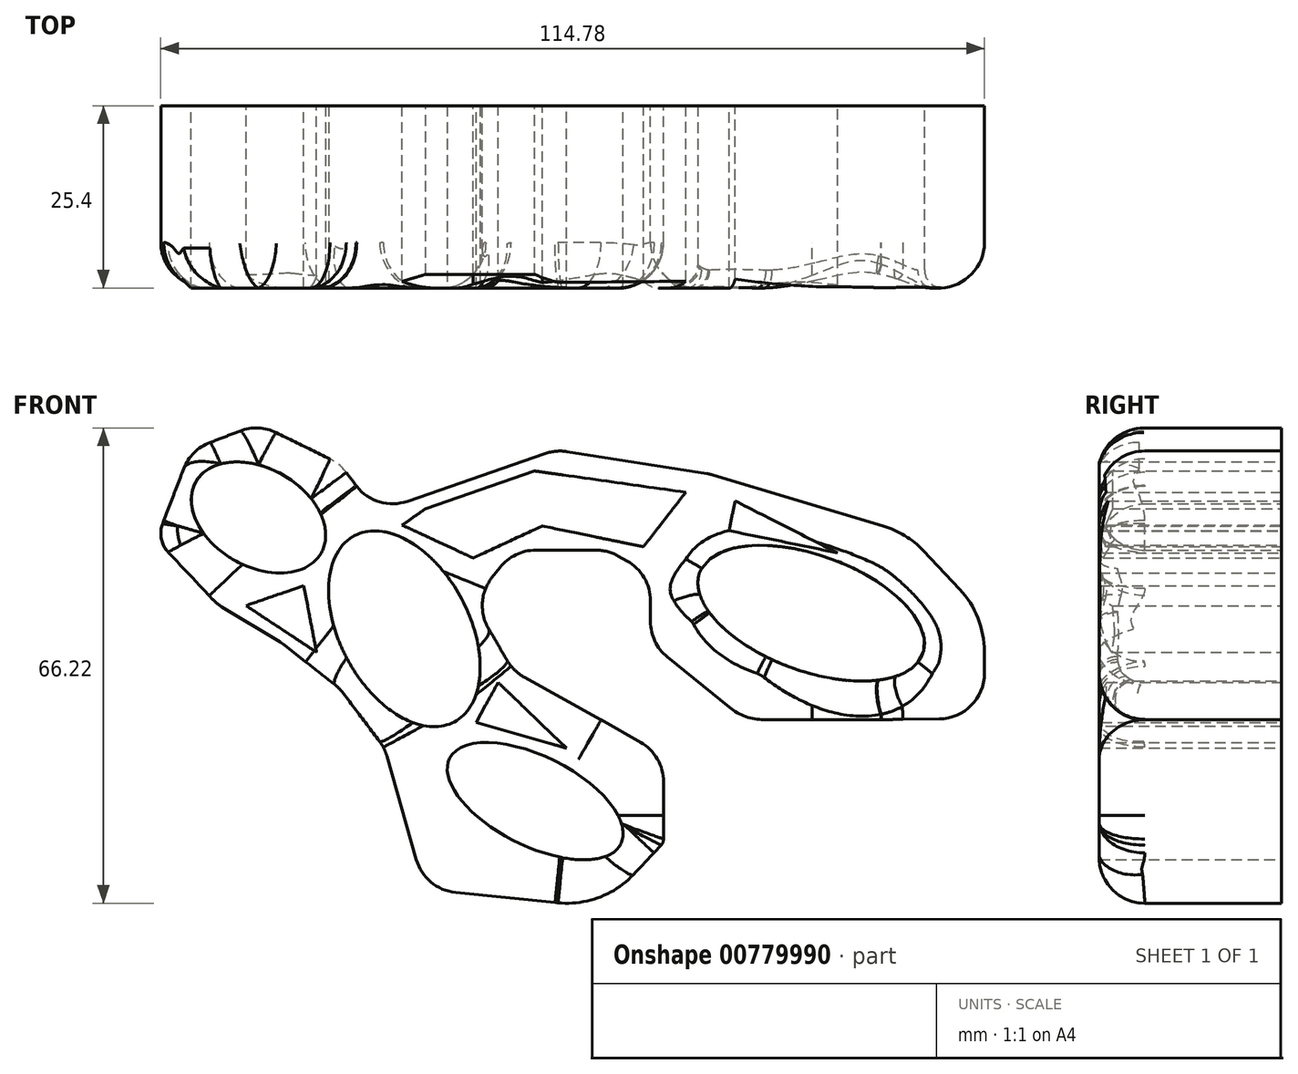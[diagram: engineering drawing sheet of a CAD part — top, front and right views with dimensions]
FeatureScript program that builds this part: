
annotation { "Feature Type Name" : "Feature", "Feature Type Description" : "" }
export const myFeature = defineFeature(function(context is Context, id is Id, definition is map)
    precondition{}
    {
        {
            var Q0;
            Q0=qCreatedBy(makeId("Front.planeOp"),FACE);
            var sketch = newSketch(context, id + "F0", { "sketchPlane" : qUnion([Q0])});
            skLineSegment(sketch, "E0", {"start": v(-14.78, 34.41) * mm, "end": v(4.4, 41.05) * mm});
            skLineSegment(sketch, "E1", {"start": v(7.47, 41.33) * mm, "end": v(26.93, 38.26) * mm});
            skLineSegment(sketch, "E2", {"start": v(27.76, 38.07) * mm, "end": v(51.5, 30.97) * mm});
            skLineSegment(sketch, "E3", {"start": v(57.1, 27.52) * mm, "end": v(62.16, 22.16) * mm});
            skLineSegment(sketch, "E4", {"start": v(65.62, 13.45) * mm, "end": v(65.62, 10.43) * mm});
            skLineSegment(sketch, "E5", {"start": v(59.35, 4.08) * mm, "end": v(51.25, 3.98) * mm});
            skLineSegment(sketch, "E6", {"start": v(51.17, 3.98) * mm, "end": v(34.9, 3.98) * mm});
            skLineSegment(sketch, "E7", {"start": v(30.1, 5.68) * mm, "end": v(21.43, 12.72) * mm});
            skLineSegment(sketch, "E8", {"start": v(19.08, 17.65) * mm, "end": v(19.08, 20.54) * mm});
            skLineSegment(sketch, "E9", {"start": v(15.83, 26.08) * mm, "end": v(14.58, 26.78) * mm});
            skLineSegment(sketch, "E10", {"start": v(11.48, 27.6) * mm, "end": v(3.1, 27.6) * mm});
            skLineSegment(sketch, "E11", {"start": v(-1.9, 25.16) * mm, "end": v(-3, 23.77) * mm});
            skLineSegment(sketch, "E12", {"start": v(-3.47, 16.64) * mm, "end": v(-0.88, 12.22) * mm});
            skLineSegment(sketch, "E13", {"start": v(1.52, 9.88) * mm, "end": v(12.13, 4) * mm});
            skLineSegment(sketch, "E14", {"start": v(12.2, 3.96) * mm, "end": v(17.71, 0.8) * mm});
            skLineSegment(sketch, "E15", {"start": v(20.91, -4.7) * mm, "end": v(20.91, -12.65) * mm});
            skLineSegment(sketch, "E16", {"start": v(20.57, -13.52) * mm, "end": v(16.72, -17.6) * mm});
            skLineSegment(sketch, "E17", {"start": v(6.21, -21.54) * mm, "end": v(-8.07, -20.1) * mm});
            skLineSegment(sketch, "E18", {"start": v(-13.54, -15.53) * mm, "end": v(-17.63, -1.14) * mm});
            skLineSegment(sketch, "E19", {"start": v(-18.67, 0.95) * mm, "end": v(-23.72, 7.65) * mm});
            skLineSegment(sketch, "E20", {"start": v(-24.87, 8.83) * mm, "end": v(-31.95, 14.38) * mm});
            skLineSegment(sketch, "E21", {"start": v(-32.58, 14.82) * mm, "end": v(-40.6, 19.68) * mm});
            skLineSegment(sketch, "E22", {"start": v(-41.92, 20.75) * mm, "end": v(-48.11, 27.3) * mm});
            skLineSegment(sketch, "E23", {"start": v(-48.9, 31.28) * mm, "end": v(-45.96, 38.94) * mm});
            skLineSegment(sketch, "E24", {"start": v(-42.31, 42.58) * mm, "end": v(-38.13, 44.2) * mm});
            skLineSegment(sketch, "E25", {"start": v(-33.06, 43.97) * mm, "end": v(-25.6, 40.32) * mm});
            skLineSegment(sketch, "E26", {"start": v(-23.3, 38.42) * mm, "end": v(-21.94, 36.6) * mm});
            skPoint(sketch, "E27.visualSharp", {"position": v(-35.55, 45.19) * mm});
            skArc(sketch, "E27.filletArc", {"start": v(-33.06, 43.97) * mm, "mid": v(-35.57, 44.6) * mm, "end": v(-38.13, 44.2) * mm});
            skPoint(sketch, "E28.visualSharp", {"position": v(-24.22, 39.64) * mm});
            skArc(sketch, "E28.filletArc", {"start": v(-23.3, 38.42) * mm, "mid": v(-24.34, 39.5) * mm, "end": v(-25.6, 40.32) * mm});
            skPoint(sketch, "E29.visualSharp", {"position": v(-19.16, 32.9) * mm});
            skArc(sketch, "E29.filletArc", {"start": v(-21.94, 36.6) * mm, "mid": v(-18.72, 34.34) * mm, "end": v(-14.78, 34.41) * mm});
            skPoint(sketch, "E30.visualSharp", {"position": v(5.9, 41.57) * mm});
            skArc(sketch, "E30.filletArc", {"start": v(7.47, 41.33) * mm, "mid": v(5.92, 41.38) * mm, "end": v(4.4, 41.05) * mm});
            skPoint(sketch, "E31.visualSharp", {"position": v(27.35, 38.2) * mm});
            skArc(sketch, "E31.filletArc", {"start": v(27.76, 38.07) * mm, "mid": v(27.35, 38.18) * mm, "end": v(26.93, 38.26) * mm});
            skPoint(sketch, "E32.visualSharp", {"position": v(54.77, 30) * mm});
            skArc(sketch, "E32.filletArc", {"start": v(57.1, 27.52) * mm, "mid": v(54.54, 29.62) * mm, "end": v(51.5, 30.97) * mm});
            skPoint(sketch, "E33.visualSharp", {"position": v(65.62, 18.49) * mm});
            skArc(sketch, "E33.filletArc", {"start": v(65.62, 13.45) * mm, "mid": v(64.73, 18.13) * mm, "end": v(62.16, 22.16) * mm});
            skPoint(sketch, "E34.visualSharp", {"position": v(65.62, 4.16) * mm});
            skArc(sketch, "E34.filletArc", {"start": v(59.35, 4.08) * mm, "mid": v(63.8, 5.97) * mm, "end": v(65.62, 10.43) * mm});
            skPoint(sketch, "E35.visualSharp", {"position": v(51.21, 3.98) * mm});
            skArc(sketch, "E35.filletArc", {"start": v(51.17, 3.98) * mm, "mid": v(51.21, 3.98) * mm, "end": v(51.25, 3.98) * mm});
            skPoint(sketch, "E36.visualSharp", {"position": v(32.2, 3.98) * mm});
            skArc(sketch, "E36.filletArc", {"start": v(30.1, 5.68) * mm, "mid": v(32.36, 4.41) * mm, "end": v(34.9, 3.98) * mm});
            skPoint(sketch, "E37.visualSharp", {"position": v(19.08, 14.62) * mm});
            skArc(sketch, "E37.filletArc", {"start": v(19.08, 17.65) * mm, "mid": v(19.7, 14.92) * mm, "end": v(21.43, 12.72) * mm});
            skPoint(sketch, "E38.visualSharp", {"position": v(19.08, 24.26) * mm});
            skArc(sketch, "E38.filletArc", {"start": v(19.08, 20.54) * mm, "mid": v(18.21, 23.75) * mm, "end": v(15.83, 26.08) * mm});
            skPoint(sketch, "E39.visualSharp", {"position": v(13.13, 27.6) * mm});
            skArc(sketch, "E39.filletArc", {"start": v(14.58, 26.78) * mm, "mid": v(13.08, 27.39) * mm, "end": v(11.48, 27.6) * mm});
            skPoint(sketch, "E40.visualSharp", {"position": v(0, 27.6) * mm});
            skArc(sketch, "E40.filletArc", {"start": v(3.1, 27.6) * mm, "mid": v(0.31, 26.95) * mm, "end": v(-1.9, 25.16) * mm});
            skPoint(sketch, "E41.visualSharp", {"position": v(-5.66, 20.36) * mm});
            skArc(sketch, "E41.filletArc", {"start": v(-3, 23.77) * mm, "mid": v(-4.33, 20.28) * mm, "end": v(-3.47, 16.64) * mm});
            skPoint(sketch, "E42.visualSharp", {"position": v(0, 10.72) * mm});
            skArc(sketch, "E42.filletArc", {"start": v(-0.88, 12.22) * mm, "mid": v(0.16, 10.9) * mm, "end": v(1.52, 9.88) * mm});
            skPoint(sketch, "E43.visualSharp", {"position": v(12.17, 3.98) * mm});
            skArc(sketch, "E43.filletArc", {"start": v(12.2, 3.96) * mm, "mid": v(12.17, 3.98) * mm, "end": v(12.13, 4) * mm});
            skPoint(sketch, "E44.visualSharp", {"position": v(20.91, -1.02) * mm});
            skArc(sketch, "E44.filletArc", {"start": v(20.91, -4.7) * mm, "mid": v(20.05, -1.52) * mm, "end": v(17.71, 0.8) * mm});
            skPoint(sketch, "E45.visualSharp", {"position": v(20.91, -13.16) * mm});
            skArc(sketch, "E45.filletArc", {"start": v(20.57, -13.52) * mm, "mid": v(20.82, -13.12) * mm, "end": v(20.91, -12.65) * mm});
            skPoint(sketch, "E46.visualSharp", {"position": v(12.44, -22.16) * mm});
            skArc(sketch, "E46.filletArc", {"start": v(6.21, -21.54) * mm, "mid": v(11.93, -20.8) * mm, "end": v(16.72, -17.6) * mm});
            skPoint(sketch, "E47.visualSharp", {"position": v(-12.37, -19.68) * mm});
            skArc(sketch, "E47.filletArc", {"start": v(-13.54, -15.53) * mm, "mid": v(-11.51, -18.66) * mm, "end": v(-8.07, -20.1) * mm});
            skPoint(sketch, "E48.visualSharp", {"position": v(-17.95, 0) * mm});
            skArc(sketch, "E48.filletArc", {"start": v(-17.63, -1.14) * mm, "mid": v(-18.05, -0.05) * mm, "end": v(-18.67, 0.95) * mm});
            skPoint(sketch, "E49.visualSharp", {"position": v(-24.22, 8.31) * mm});
            skArc(sketch, "E49.filletArc", {"start": v(-23.72, 7.65) * mm, "mid": v(-24.26, 8.28) * mm, "end": v(-24.87, 8.83) * mm});
            skPoint(sketch, "E50.visualSharp", {"position": v(-32.25, 14.62) * mm});
            skArc(sketch, "E50.filletArc", {"start": v(-31.95, 14.38) * mm, "mid": v(-32.26, 14.61) * mm, "end": v(-32.58, 14.82) * mm});
            skPoint(sketch, "E51.visualSharp", {"position": v(-41.33, 20.12) * mm});
            skArc(sketch, "E51.filletArc", {"start": v(-41.92, 20.75) * mm, "mid": v(-41.3, 20.17) * mm, "end": v(-40.6, 19.68) * mm});
            skPoint(sketch, "E52.visualSharp", {"position": v(-49.77, 29.04) * mm});
            skArc(sketch, "E52.filletArc", {"start": v(-48.9, 31.28) * mm, "mid": v(-49.08, 29.17) * mm, "end": v(-48.11, 27.3) * mm});
            skPoint(sketch, "E53.visualSharp", {"position": v(-44.95, 41.57) * mm});
            skArc(sketch, "E53.filletArc", {"start": v(-42.31, 42.58) * mm, "mid": v(-44.52, 41.15) * mm, "end": v(-45.96, 38.94) * mm});
            skEllipse(sketch, "E54", {"center": v(-35.55, 32.15) * mm, "majorRadius": 10.05 * mm, "minorRadius": 6.84 * mm, "majorAxis": v(0.87, -0.5)});
            skEllipse(sketch, "E55", {"center": v(3.02, -7.38) * mm, "majorRadius": 13.34 * mm, "minorRadius": 6.25 * mm, "majorAxis": v(-0.9, 0.45)});
            skEllipse(sketch, "E56", {"center": v(-15.21, 16.64) * mm, "majorRadius": 14.72 * mm, "minorRadius": 9 * mm, "majorAxis": v(-0.47, 0.88)});
            skEllipse(sketch, "E57", {"center": v(41.48, 18.8) * mm, "majorRadius": 16.54 * mm, "minorRadius": 8.07 * mm, "majorAxis": v(-0.94, 0.34)});
            skLineSegment(sketch, "E58", {"start": v(-12.26, 33.37) * mm, "end": v(2.93, 38.63) * mm});
            skLineSegment(sketch, "E59", {"start": v(2.93, 38.63) * mm, "end": v(24.01, 35.66) * mm});
            skLineSegment(sketch, "E60", {"start": v(24.01, 35.66) * mm, "end": v(18.1, 28.07) * mm});
            skLineSegment(sketch, "E61", {"start": v(18.1, 28.07) * mm, "end": v(4, 30.96) * mm});
            skLineSegment(sketch, "E62", {"start": v(4, 30.96) * mm, "end": v(-5.63, 26.5) * mm});
            skLineSegment(sketch, "E63", {"start": v(-5.63, 26.5) * mm, "end": v(-15.51, 31.08) * mm});
            skLineSegment(sketch, "E64", {"start": v(-15.51, 31.08) * mm, "end": v(-12.26, 33.37) * mm});
            skLineSegment(sketch, "E65", {"start": v(-2.14, 9.15) * mm, "end": v(-5.21, 3.6) * mm});
            skLineSegment(sketch, "E66", {"start": v(-5.21, 3.6) * mm, "end": v(7.38, 0) * mm});
            skLineSegment(sketch, "E67", {"start": v(7.38, 0) * mm, "end": v(-2.14, 9.15) * mm});
            skLineSegment(sketch, "E68", {"start": v(30.88, 34.45) * mm, "end": v(30.03, 30.31) * mm});
            skLineSegment(sketch, "E69", {"start": v(30.03, 30.31) * mm, "end": v(45.16, 27.2) * mm});
            skLineSegment(sketch, "E70", {"start": v(45.16, 27.2) * mm, "end": v(30.88, 34.45) * mm});
            skLineSegment(sketch, "E71", {"start": v(-29.25, 22.64) * mm, "end": v(-37.27, 19.87) * mm});
            skLineSegment(sketch, "E72", {"start": v(-37.27, 19.87) * mm, "end": v(-27.44, 13.37) * mm});
            skLineSegment(sketch, "E73", {"start": v(-27.44, 13.37) * mm, "end": v(-29.25, 22.64) * mm});
            skSolve(sketch);
        }
        {
            var Q0;
            Q0 = qSketchRegion(id + "F0", true);
            extrude(context, id + "F1", {"entities" : qUnion([Q0]), "depth" : 25.4 * mm, "offsetDistance" : 25.4 * mm});
        }
        {
            var Q0;
            Q0=makeQuery(id+"F1.opExtrude","CAP_EDGE",EDGE,{"disambiguationData":[OSD([sQuery(id+"F0.wireOp",EDGE,"E2")])],"isStart":false});
            fillet(context, id + "F2", {"entities" : qUnion([Q0]), "radius" : 6.35 * mm, "tangentPropagation" : true, "allowEdgeOverflow" : false});
        }
        {
            var Q0;
            Q0=makeQuery(id+"F1.opExtrude","CAP_EDGE",EDGE,{"disambiguationData":[OSD([sQuery(id+"F0.wireOp",EDGE,"E57")])],"isStart":false});
            fillet(context, id + "F3", {"entities" : qUnion([Q0]), "radius" : 2.54 * mm, "tangentPropagation" : true, "allowEdgeOverflow" : false});
        }
    });
